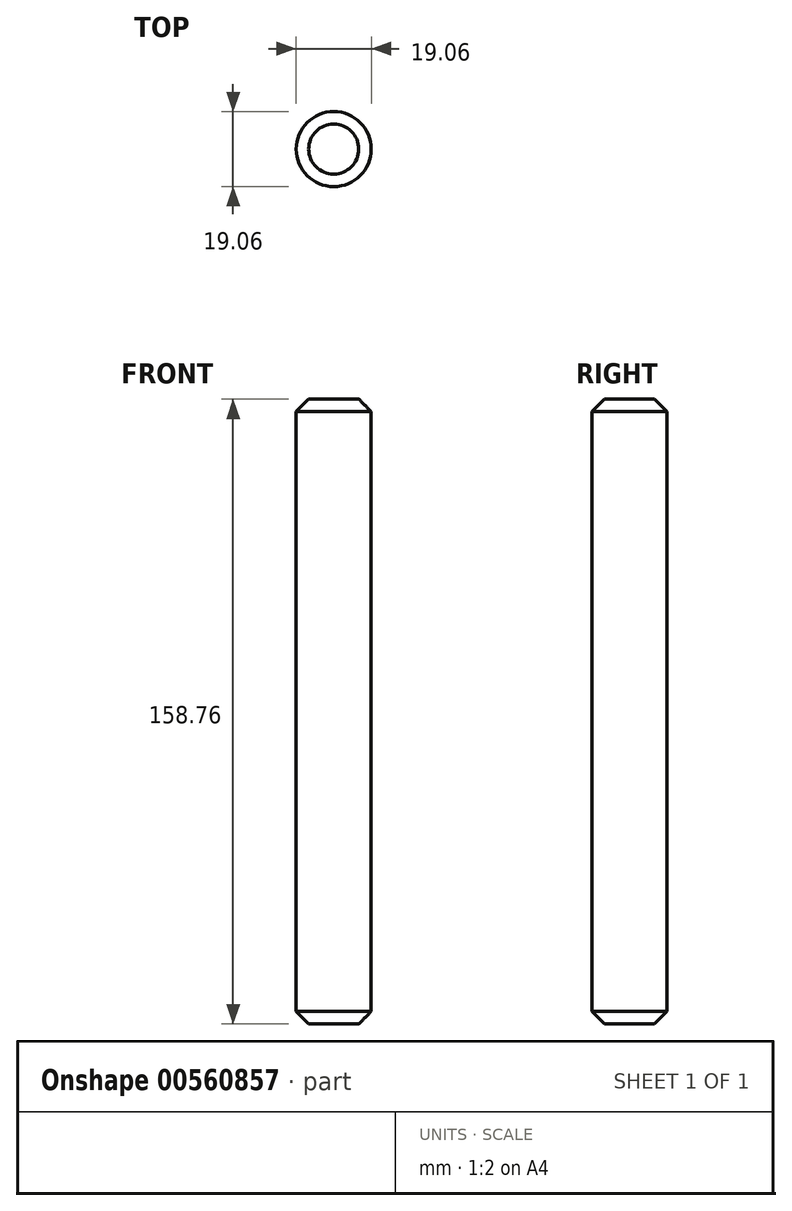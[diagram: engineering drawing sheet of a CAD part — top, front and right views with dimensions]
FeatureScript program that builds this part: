
annotation { "Feature Type Name" : "Feature", "Feature Type Description" : "" }
export const myFeature = defineFeature(function(context is Context, id is Id, definition is map)
    precondition{}
    {
        {
            var Q0;
            Q0=qCreatedBy(makeId("Top.planeOp"),FACE);
            var sketch = newSketch(context, id + "F0", { "sketchPlane" : qUnion([Q0])});
            skCircle(sketch, "E0", {"center": v(0, 0) * mm, "radius": 9.53 * mm});
            skSolve(sketch);
        }
        {
            var Q0;
            Q0 = qSketchRegion(id + "F0", true);
            extrude(context, id + "F1", {"entities" : qUnion([Q0]), "depth" : 158.75 * mm, "offsetDistance" : 25.4 * mm, "symmetric" : true});
        }
        {
            var Q0;
            Q0=makeQuery(id+"F1.opExtrude","CAP_EDGE",EDGE,{"disambiguationData":[OSD([sQuery(id+"F0.wireOp",EDGE,"E0")])],"isStart":false});
            var Q1;
            Q1=makeQuery(id+"F1.opExtrude","CAP_EDGE",EDGE,{"disambiguationData":[OSD([sQuery(id+"F0.wireOp",EDGE,"E0")])],"isStart":true});
            chamfer(context, id + "F2", {"entities" : qUnion([Q0, Q1]), "width" : 3.17 * mm, "tangentPropagation" : true});
        }
    });
